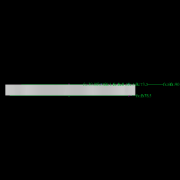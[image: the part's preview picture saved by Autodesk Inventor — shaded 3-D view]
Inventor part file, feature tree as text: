
AUTODESK INVENTOR PART (.ipt)
format: ipt  version: 2022.2 (Build 262287010, 287A)  size: 1,148,416 bytes
history: native  units: mm
features: extrude x20, sketch x19, pattern_circular x15, other x14, revolve x7, hole x7, move_body x4, fillet x2, draft x2
ambient origin geometry x8: Origin, YZ Plane, XZ Plane, XY Plane, X Axis, Y Axis, Z Axis, Center Point
bodies: Solid1 (feature_tree), Solid2 (feature_tree), Solid3 (feature_tree), Solid4 (feature_tree), Solid5 (feature_tree)
feature tree (90):
  sketch  "Sketch7"  dims[d21=0.5mm]
  other  "Roller1"
  other  "Roller2"
  sketch  "Sketch22"  dims[d39=0.05mm]
  sketch  "Sketch2"  dims[d17=0.05mm]
  sketch  "Sketch23"  dims[d41=0.05mm]
  other  "RevRoller1"
  fillet  "Fillet1"  Radius=0.05mm
  pattern_circular  "Circular Pattern13"  Count=6  [1 undecoded]
  move_body  "Move Body7"
  revolve  "Revolution13"  Angle=30.0deg
  fillet  "Fillet3"  [1 undecoded]
  pattern_circular  "Circular Pattern14"  [2 undecoded]
  move_body  "Move Body6"
  revolve  "Revolution14"  Angle=90.0deg
  extrude  "Extrusion23"  Depth=0.5mm
  other  "OuterRim_Top2"
  other  "OuterRim_Bottom2"
  extrude  "Extrusion9"  Depth=0.5mm
  sketch  "Sketch24"  dims[d42=0.5mm]
  extrude  "Extrusion10"  Depth=0.5mm
  extrude  "Extrusion11"  Depth=0.5mm
  pattern_circular  "Circular Pattern15"  [2 undecoded]
  sketch  "Sketch25"  dims[d43=0.5mm]
  extrude  "Extrusion12"  Depth=0.5mm
  extrude  "Extrusion14"  Depth=0.5mm
  extrude  "Extrusion15"  Depth=0.5mm
  pattern_circular  "Circular Pattern16"  [2 undecoded]
  extrude  "Extrusion16"  Depth=0.5mm
  extrude  "Extrusion17"  Depth=0.5mm
  hole  "Hole9"  [1 undecoded]
  pattern_circular  "Circular Pattern17"  [2 undecoded]
  sketch  "Sketch27"  dims[d45=0.5mm]
  hole  "Hole10"  [1 undecoded]
  hole  "Hole11"  [1 undecoded]
  pattern_circular  "Circular Pattern18"  [2 undecoded]
  extrude  "Extrusion18"  Depth=0.5mm
  extrude  "Extrusion19"  Depth=0.5mm
  pattern_circular  "Circular Pattern19"  [2 undecoded]
  sketch  "Sketch28"  dims[d46=0.5mm]
  extrude  "Extrusion20"  Depth=0.5mm
  extrude  "Extrusion22"  Depth=0.5mm
  pattern_circular  "Circular Pattern21"  [2 undecoded]
  draft  "FaceDraft2"
  other  "InnerRim"
  other  "OuterRim_Top"
  other  "OuterRim_Bottom"
  extrude  "Extrusion2"  TaperAngle=90.0deg  [1 undecoded]
  sketch  "Sketch13"  dims[d24=0.5mm]
  extrude  "Extrusion3"  TaperAngle=30.0deg  [1 undecoded]
  sketch  "Sketch15"  dims[d29=360.0deg d30=60.0mm]
  extrude  "Extrusion4"  TaperAngle=90.0deg  [1 undecoded]
  extrude  "Extrusion5"  Depth=0.5mm
  pattern_circular  "Circular Pattern6"  [2 undecoded]
  sketch  "Sketch16"  dims[d31=360.0deg d35=30.0deg d36=90.0deg]
  extrude  "Extrusion6"  Depth=55.5mm
  extrude  "Extrusion7"  TaperAngle=90.0deg  [1 undecoded]
  pattern_circular  "Circular Pattern7"  Angle=90.0deg  [1 undecoded]
  hole  "Hole5"  [1 undecoded]
  pattern_circular  "Circular Pattern9"  [2 undecoded]
  draft  "FaceDraft1"
  hole  "Hole6"  [1 undecoded]
  pattern_circular  "Circular Pattern10"  Count=360  [1 undecoded]
  hole  "Hole7"  [1 undecoded]
  pattern_circular  "Circular Pattern11"  [2 undecoded]
  hole  "Hole8"  [1 undecoded]
  extrude  "Extrusion8"  TaperAngle=0.0deg  [1 undecoded]
  pattern_circular  "Circular Pattern12"  [2 undecoded]
  sketch  "Sketch8"  dims[d22=0.5mm]
  sketch  "Sketch9"  dims[d23=0.5mm]
  revolve  "Revolution4"  [1 undecoded]
  move_body  "Move Body4"
  revolve  "Revolution5"  [1 undecoded]
  sketch  "Sketch5"  dims[d19=0.5mm]
  sketch  "Sketch6"  dims[d20=0.5mm]
  revolve  "Revolution3"  [1 undecoded]
  sketch  "Sketch4"  dims[d18=0.05mm]
  revolve  "Revolution1"  [1 undecoded]
  pattern_circular  "Circular Pattern1"  Count=9  [1 undecoded]
  move_body  "Move Body3"
  revolve  "Revolution2"  Angle=360.0deg
  other  "2D Equation Curve1"
  sketch  "Sketch14"  dims[d28=2.0mm]
  other  "Work Axis1"
  other  "Work Axis2"
  other  "Work Axis3"
  other  "Work Axis4"
  other  "Work Axis5"
  sketch  "Sketch26"  dims[d44=0.5mm]
  sketch  "Sketch29"  dims[d47=0.5mm d48=2.0mm d50=90.0deg d56=14.029612mm d57=4.025mm d90=16.473921mm d107=0.05mm d108=0.05mm d109=0.05mm d110=0.05mm d112=0.5mm d113=0.5mm d114=0.5mm d115=14.644822mm d116=14.607374mm d117=1.0mm d118=0.05mm d119=0.05mm d120=0.05mm d121=0.05mm d122=0.5mm d123=0.5mm d124=14.644822mm d125=14.607374mm d126=1.0mm d127=90.0deg d128=30.0deg d129=90.0deg d167=8.972256mm d173=10.814812mm d201=55.5mm d202=90.0deg d203=90.0deg d204=90.0deg d218=55.5mm d226=5.4mm d232=0.0mm d233=3600.0mm d234=10.502mm d235=0.0mm d243=1.902mm d244=0.0mm d246=2.75mm d247=5.251mm d248=0.0mm d249=3.0mm d250=0.0mm d251=90.0mm d252=360.0deg d254=2.75mm d255=3.0mm d256=5.251mm d257=0.0mm d258=3.0mm d259=0.0mm d260=90.0mm d261=360.0deg d277=76.5mm d281=73.5mm d282=24.65mm d283=6.0mm d284=4.0mm d285=2.0mm d286=90.0deg d287=5.251mm d288=0.0mm d289=60.0mm d290=360.0deg d292=0.436332mm d293=60.0mm d294=90.0mm d295=3.0mm d296=6.0mm d297=5.5mm d298=3.0mm d299=90.0deg d300=5.251mm d301=0.0mm d302=60.0mm d303=360.0deg d305=30.0deg d306=73.5mm d307=24.65mm d308=6.0mm d309=5.5mm d310=3.0mm d311=90.0deg d312=5.251mm d313=0.0mm d314=60.0mm d315=360.0deg d317=90.0mm d318=60.0mm d319=30.0deg d320=5.4mm d321=5.4mm d322=3.0mm d323=6.0mm d324=5.5mm d325=3.0mm d326=90.0deg d327=5.251mm d328=0.0mm d329=2.4mm d330=0.0mm d331=60.0mm d332=360.0deg d343=17.307186mm d344=17.309884mm d345=0.025mm d346=0.025mm d347=0.1mm d348=0.1mm d349=17.309884mm d350=17.307186mm d351=0.025mm d352=0.025mm d354=0.1mm d355=17.307186mm d356=17.309884mm d357=1.0mm d358=90.0deg d359=0.5mm d360=60.0mm d361=360.0deg d363=30.0deg d367=8.1mm d369=4.014775mm d370=0.1mm d371=1.0mm d372=30.0deg d373=90.0deg d374=0.5mm d375=60.0mm d376=360.0deg d378=90.0deg d379=0.1mm d380=0.1mm d381=0.1mm d382=0.1mm d383=0.1mm d384=10.502mm d385=0.0mm d386=0.0mm d391=1.0mm d392=55.5mm d393=1.5mm d394=1.5mm d395=1.5mm d396=1.5mm d397=90.0deg d398=90.0deg d399=90.0deg d400=55.5mm d401=10.502mm d402=0.0mm d403=2.75mm d404=1.5mm d405=10.502mm d406=0.0mm d407=3.0mm d408=0.0mm d409=90.0mm d410=360.0deg d412=5.4mm d413=5.251mm d414=0.0mm d417=5.4mm d418=2.4mm d419=0.0mm d420=2.4mm d421=0.0mm d422=90.0mm d423=360.0deg d425=60.0mm d426=90.0mm d427=1.5mm d428=1.5mm d429=5.4mm d430=5.4mm d431=5.251mm d432=0.0mm d433=2.4mm d434=0.0mm d435=30.0deg d436=73.5mm d437=24.65mm d438=6.0mm d439=4.0mm d440=2.0mm d441=90.0deg d442=5.251mm d443=0.0mm d444=60.0mm d445=360.0deg d447=3.0mm d448=6.0mm d449=5.5mm d450=3.0mm d451=90.0deg d452=5.251mm d453=0.0mm d454=24.65mm d455=6.0mm d456=5.5mm d457=3.0mm d458=90.0deg d459=5.251mm d460=0.0mm d461=60.0mm d462=360.0deg d464=5.251mm d465=0.0mm d466=3.0mm d467=0.0mm d468=90.0mm d469=360.0deg d472=1.5mm d474=5.251mm d475=0.0mm d481=3.0mm d482=0.0mm d483=90.0mm d484=360.0deg d486=0.436332mm d487=0.0mm d488=15.0mm d489=0.0mm d490=0.0mm d491=2.0mm d49=0.872665mm d51=0.872665mm d52=0.872665mm d236=0.5mm d237=0.872665mm d238=0.5mm d239=0.872665mm d291=0.0625mm d415=0.5mm d416=0.872665mm d471=0.5mm d473=0.5mm]
note: 43 required parameter values undecoded (feature->parameter linkage not recoverable at this tier; creation-order binding heuristic only, values carry confidence <= 0.55)